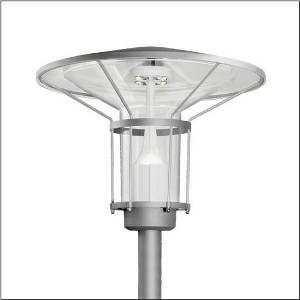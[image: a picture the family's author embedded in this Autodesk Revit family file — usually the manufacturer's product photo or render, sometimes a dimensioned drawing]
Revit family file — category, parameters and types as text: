
# Revit family: laterne_classic_iq___st1_2a_5xa5245af14h_9f1a
name_source: partatom
category: Lighting Fixtures
units: mm (PartAtom-declared; Revit-internal decimal feet)

## family parameters
Cut with Voids When Loaded = No
Host = Face
Light Source = No
Part Type = Normal
Room Calculation Point = No
Round Connector Dimension = Use Diameter
Shared = No

## types (1)
- --- (1 x LED, 1380 lm, 12.9 W, 2200K)
    Apparent Load = 13 VA
    CIE Flux Codes = 21 60 93 97 100
    Color Rendering = 70
    Color Temperature = 2200K
    Default Elevation = 1800 mm
    Description = Lantern Classic iQ, mast luminaire, Module 540 iQ-SR, primary light control with 3 zone facetted reflector, of plastic, silver coated, highly specular, structured, primary optical cover: cover, of PMMA, transparent, light distribution: ST1.2a, light emission: direct distribution, primary light characteristic: asymmetric, installation type: post-top, LED, High Power LED, rated luminous flux: 1.380lm, luminous efficacy: 107lm/W, light colour: 722, colour temperature: 2200K, control gear: iQ Street-Remote, control: pre-setting: logarithmic dimming characteristic, Street-Remote, Auto-Match, Temp-Guard, Lumen-Switch, Night-Set, Smart-Wire, Light-Fading, Desk-Remote (wireless, voltage-free reading and setting of iQ features in the workshop via application-optimized NFC function/RFID function), optimised constant luminous flux control (CLO 2.0), with terminal, 6-pole, max. 2.5mm², mains connection: 230..240V, AC, 50/60Hz, start of lifetime: 13W, end of service life: 13W, reduction: 6W, luminaire housing, upper part, of glass-fibre reinforced polyester, coated, Siteco® metallic grey (DB 702S), diameter: 750mm, height: 596mm, spigot size: d x l = 76 x 70mm (post-top) | with reducer (optional accessory) 60 x 70mm, mounting height: 3..5m, post-top mast mounting element, of diecast aluminium, coated, Siteco® metallic grey (DB 702S), Module 540 iQ-SR, traffic white (RAL 9016), equipment: standard, protection rating (complete): IP65, insulation class (complete): insulation class II (safety insulation), certification: CE, ENEC, VDE, packaging unit: 1 piece

Light Distribution: ST1.2a
    Height = 596 mm
    Lamp = 1 x LED
    Lamp Light Flux = 1380 lm
    Lamp Power = 12.9 W
    Lamp count = 1
    Length = 750 mm
    Luminous efficacy = 107 lm/W
    Manufacturer = Siteco
    ModVariant = No
    Model = 5XA5245AF14H
    Number of Poles = 1
    OnlyDefault = Yes
    Power Factor = 1
    Product Name = Laterne Classic iQ | ST1.2a
    Product group = mast luminaire | pylon top
    ProductGroupID = 6100
    Protection Class = Protection class II
    Protection Degree = IP 65
    RLX_Detail_Level = 1
    RLX_Emergency_Light_Flux = 0 lm
    RLX_Emergency_Type = 0
    RLX_Emergency_Type_DB = No
    RlxData = <blob elided: 91817 chars, md5=a195a6db>
    Socket = socket
    Standby Power = 0 W
    System Light Flux = 1380 lm
    System Power = 13 W
    Type Comments = factory setting: luminous flux: 100 % | dim-lin: 254 | 516 mA
    Type Image = l_1006052.jpg
    URL = http://relux.com
    VarID = @adj_181873
    Voltage = 0 V
    Weight = 0.00 kg
    Width = 0 mm  [stored 0 ft]

note: [stored X ft] marks values corroborated as IEEE doubles in the binary element streams (Revit-internal decimal feet)

## geometry (parser evidence)
native form markers: Blend x4, Sweep x9
no freeform markers — native parametric forms only
